# Revit family: Sanext_Сгон разъемный прямой HP
name_source: partatom
category: Соединительные детали трубопроводов
revit_build: Autodesk Revit 2017 (Build: 20171027_0315(x64)
units: mm (PartAtom-declared; Revit-internal decimal feet)

## family parameters
Всегда вертикально = Да
На основе рабочей плоскости = Нет
Общий = Нет
При загрузке вырезать с полостями = Нет
Размер круглого соединителя = Использовать радиус
Тип детали = Отвод

## types (1)
- Sanext_Сгон разъемный прямой HP
    ADSK_Единица измерения = шт
    ADSK_Завод-изготовитель = ООО САНЕКСТ.ПРО
    ADSK_Код изделия = 8792
    ADSK_Масса = 0
    ADSK_Материал наименование = DZR латунь
    ADSK_Наименование = Сгон разъемный прямой HP
    D = 20 мм
    L = 40 мм
    R = 10 мм
    URL = http://sanext.ru
    z = 1
    Гайка = 30 мм
    Группа модели = Сгон разъемный
    Изготовитель = ООО САНЕКСТ.ПРО
    Материал стальной части = DZR латунь
    Описание = Сгон разъемный прямой HP
    Рабочее давление = 0.0 кПа
    Разработчик = ООО ПРОРУБИМ
    Разработчик (телефон) = +7(495)649-85-43
    Разработчик модели (URL) = http://prorubim.com
